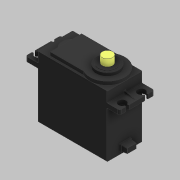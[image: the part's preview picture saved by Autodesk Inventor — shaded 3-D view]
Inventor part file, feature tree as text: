
AUTODESK INVENTOR PART (.ipt)
format: ipt  version: 2021 (Build 250183000, 183)  size: 411,136 bytes
history: native  units: mm
features: extrude x11, sketch x10, fillet x7, chamfer x5, other x2, projected_geometry x2, mirror x1
ambient origin geometry x8: Origin, YZ Plane, XZ Plane, XY Plane, X Axis, Y Axis, Z Axis, Center Point
bodies: Body1 (feature_tree)
feature tree (38):
  other  "솔리드1"
  extrude  "돌출1"  Depth=40.0mm
  other  "작업 평면1"
  extrude  "돌출2"  Depth=20.0mm
  extrude  "돌출3"  Depth=37.0mm TaperAngle=0.0deg
  extrude  "돌출4"  [1 undecoded]
  mirror  "미러1"
  extrude  "돌출5"  Depth=54.0mm
  extrude  "돌출6"  Depth=2.5mm TaperAngle=0.0deg
  sketch  "스케치7"
  extrude  "돌출7"  Depth=4.5mm
  extrude  "돌출8"  Depth=4.5mm
  extrude  "돌출9"  Depth=3.0mm
  fillet  "모깎기1"  Radius=1.0mm
  fillet  "모깎기2"  Radius=4.5mm
  chamfer  "모따기1"  [1 undecoded]
  fillet  "모깎기3"  Radius=1.4mm
  fillet  "모깎기4"  Radius=0.7mm
  fillet  "모깎기5"  Radius=10.0mm
  extrude  "돌출10"  Depth=20.0mm
  extrude  "돌출11"  Depth=18.0mm
  chamfer  "모따기2"  Distance=6.0mm
  chamfer  "모따기3"  Distance=2.0mm
  chamfer  "모따기4"  Distance=2.0mm
  chamfer  "모따기5"  Distance=4.5mm
  fillet  "모깎기6"  Radius=9.0mm
  fillet  "모깎기7"  Radius=1.7mm
  sketch  "스케치1"
  sketch  "스케치2"
  sketch  "스케치3"
  sketch  "스케치4"
  sketch  "스케치5"
  sketch  "스케치6"
  sketch  "스케치8"
  projected_geometry  "투영된 루프1"
  sketch  "스케치9"
  sketch  "스케치10"
  projected_geometry  "투영된 루프2"
note: 2 required parameter values undecoded (feature->parameter linkage not recoverable at this tier; creation-order binding heuristic only, values carry confidence <= 0.55)
